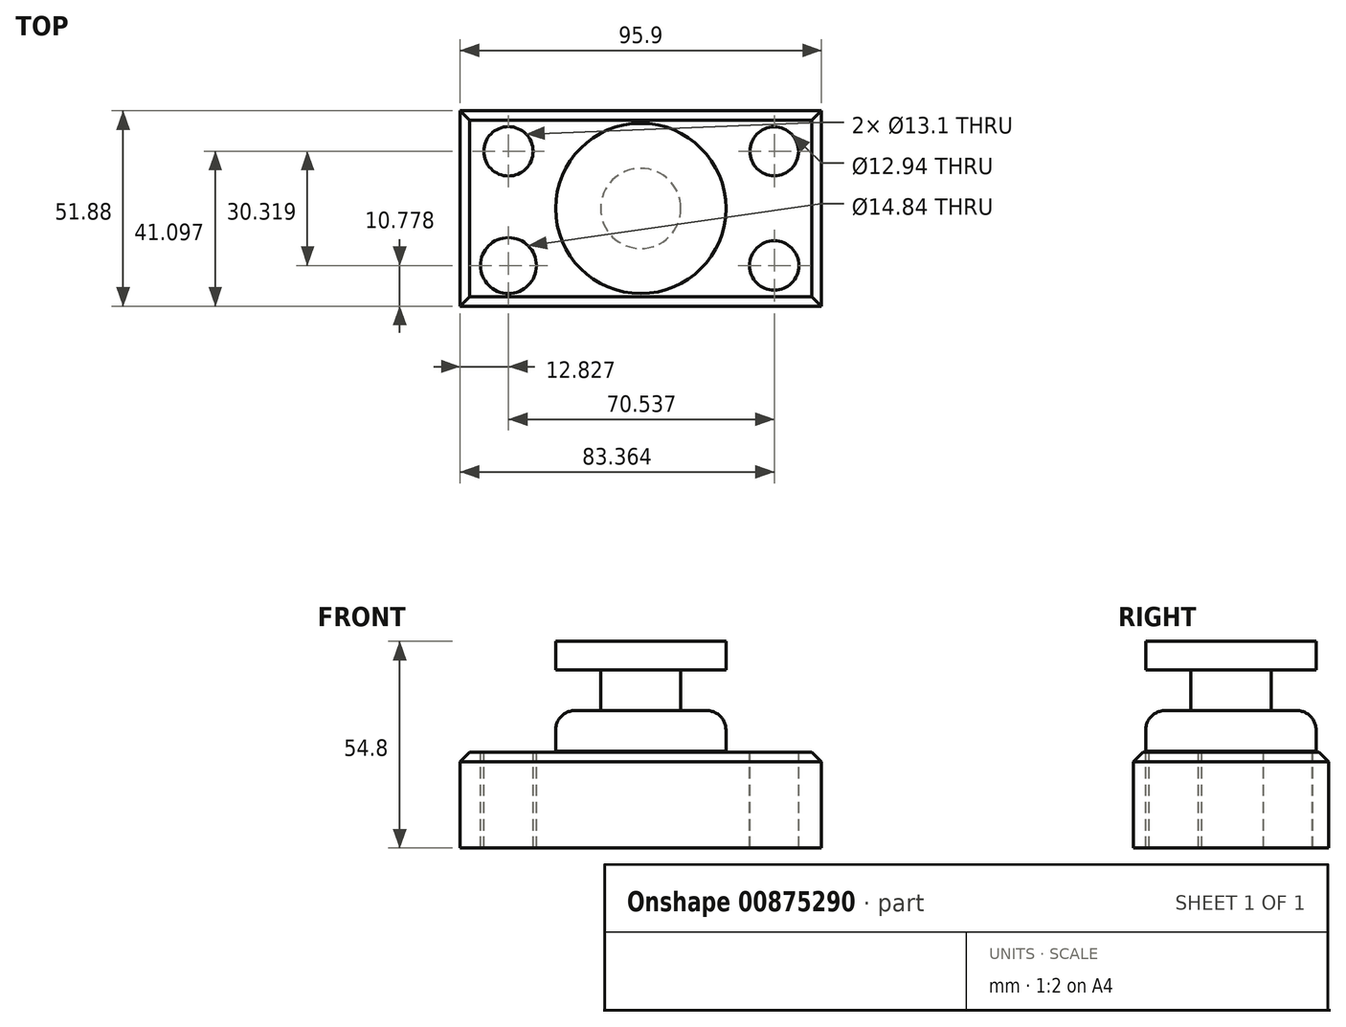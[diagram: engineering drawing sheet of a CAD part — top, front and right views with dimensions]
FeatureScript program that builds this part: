
annotation { "Feature Type Name" : "Feature", "Feature Type Description" : "" }
export const myFeature = defineFeature(function(context is Context, id is Id, definition is map)
    precondition{}
    {
        {
            var Q0;
            Q0=qCreatedBy(makeId("Top.planeOp"),FACE);
            var sketch = newSketch(context, id + "F0", { "sketchPlane" : qUnion([Q0])});
            skLineSegment(sketch, "E0.bottom", {"start": v(47.95, 25.94) * mm, "end": v(-47.95, 25.94) * mm});
            skLineSegment(sketch, "E0.top", {"start": v(47.95, -25.94) * mm, "end": v(-47.95, -25.94) * mm});
            skLineSegment(sketch, "E0.left", {"start": v(47.95, 25.94) * mm, "end": v(47.95, -25.94) * mm});
            skLineSegment(sketch, "E0.right", {"start": v(-47.95, 25.94) * mm, "end": v(-47.95, -25.94) * mm});
            skPoint(sketch, "E0.middle", {"position": v(0, 0) * mm});
            skSolve(sketch);
        }
        {
            var Q0;
            Q0=makeQuery(id+"F0.imprint","IMPRINT",FACE,{"disambiguationData":[TD([[makeQuery(id+"F0.imprint","IMPRINT",EDGE,{"derivedFrom":sQuery(id+"F0.wireOp",EDGE,"E0.bottom")}),1.0]])]});
            extrude(context, id + "F1", {"entities" : qUnion([Q0]), "depth" : 25.4 * mm, "offsetDistance" : 25.4 * mm});
        }
        {
            var Q0;
            Q0=makeQuery(id+"F1.opExtrude","CAP_FACE",FACE,{"disambiguationData":[OSD([sQuery(id+"F0.wireOp",EDGE,"E0.bottom"),sQuery(id+"F0.wireOp",EDGE,"E0.top"),sQuery(id+"F0.wireOp",EDGE,"E0.left"),sQuery(id+"F0.wireOp",EDGE,"E0.right")])],"isStart":false});
            var sketch = newSketch(context, id + "F2", { "sketchPlane" : qUnion([Q0])});
            skCircle(sketch, "E1", {"center": v(-35.12, 15.16) * mm, "radius": 6.55 * mm});
            skCircle(sketch, "E2", {"center": v(35.41, 15.16) * mm, "radius": 6.47 * mm});
            skCircle(sketch, "E3", {"center": v(-35.12, -15.16) * mm, "radius": 7.42 * mm});
            skCircle(sketch, "E4", {"center": v(35.41, -15.16) * mm, "radius": 6.55 * mm});
            skSolve(sketch);
        }
        {
            var Q0;
            Q0=makeQuery(id+"F2.imprint","IMPRINT",FACE,{"disambiguationData":[TD([[makeQuery(id+"F2.imprint","IMPRINT",EDGE,{"derivedFrom":sQuery(id+"F2.wireOp",EDGE,"E1")}),1.0]])]});
            var Q1;
            Q1=makeQuery(id+"F2.imprint","IMPRINT",FACE,{"disambiguationData":[TD([[makeQuery(id+"F2.imprint","IMPRINT",EDGE,{"derivedFrom":sQuery(id+"F2.wireOp",EDGE,"E2")}),1.0]])]});
            var Q2;
            Q2=makeQuery(id+"F2.imprint","IMPRINT",FACE,{"disambiguationData":[TD([[makeQuery(id+"F2.imprint","IMPRINT",EDGE,{"derivedFrom":sQuery(id+"F2.wireOp",EDGE,"E4")}),1.0]])]});
            var Q3;
            Q3=makeQuery(id+"F2.imprint","IMPRINT",FACE,{"disambiguationData":[TD([[makeQuery(id+"F2.imprint","IMPRINT",EDGE,{"derivedFrom":sQuery(id+"F2.wireOp",EDGE,"E3")}),1.0]])]});
            extrude(context, id + "F3", {"entities" : qUnion([Q0, Q1, Q2, Q3]), "operationType" : NewBodyOperationType.REMOVE, "oppositeDirection" : true, "depth" : 25.4 * mm, "offsetDistance" : 25.4 * mm});
        }
        {
            var Q0;
            Q0=qCreatedBy(makeId("Front.planeOp"),FACE);
            var sketch = newSketch(context, id + "F4", { "sketchPlane" : qUnion([Q0])});
            skLineSegment(sketch, "E5", {"start": v(0, 0) * mm, "end": v(0, 54.8) * mm});
            skLineSegment(sketch, "E6", {"start": v(0, 54.8) * mm, "end": v(22.59, 54.8) * mm});
            skLineSegment(sketch, "E7", {"start": v(22.59, 54.8) * mm, "end": v(22.59, 47.22) * mm});
            skLineSegment(sketch, "E8", {"start": v(22.59, 47.22) * mm, "end": v(10.64, 47.22) * mm});
            skLineSegment(sketch, "E9", {"start": v(10.64, 47.22) * mm, "end": v(10.64, 36.43) * mm});
            skLineSegment(sketch, "E10", {"start": v(10.64, 36.43) * mm, "end": v(22.59, 36.43) * mm});
            skLineSegment(sketch, "E11", {"start": v(22.59, 36.43) * mm, "end": v(22.59, 25.65) * mm});
            skLineSegment(sketch, "E12", {"start": v(22.59, 25.65) * mm, "end": v(0, 25.65) * mm});
            skSolve(sketch);
        }
        {
            var Q0;
            Q0=makeQuery(id+"F1.opExtrude","CAP_EDGE",EDGE,{"disambiguationData":[OSD([sQuery(id+"F0.wireOp",EDGE,"E0.top")])],"isStart":false});
            var Q1;
            Q1=makeQuery(id+"F1.opExtrude","CAP_EDGE",EDGE,{"disambiguationData":[OSD([sQuery(id+"F0.wireOp",EDGE,"E0.right")])],"isStart":false});
            var Q2;
            Q2=makeQuery(id+"F1.opExtrude","CAP_EDGE",EDGE,{"disambiguationData":[OSD([sQuery(id+"F0.wireOp",EDGE,"E0.left")])],"isStart":false});
            var Q3;
            Q3=makeQuery(id+"F1.opExtrude","CAP_EDGE",EDGE,{"disambiguationData":[OSD([sQuery(id+"F0.wireOp",EDGE,"E0.bottom")])],"isStart":false});
            chamfer(context, id + "F5", {"entities" : qUnion([Q0, Q1, Q2, Q3]), "width" : 2.54 * mm, "tangentPropagation" : true});
        }
        {
            var Q0;
            {var subQ0=sQuery(id+"F4.wireOp",EDGE,"E6");Q0=makeQuery(id+"F4.imprint","IMPRINT",FACE,{"disambiguationData":[TD([[makeQuery(id+"F4.imprint","IMPRINT",EDGE,{"derivedFrom":subQ0}),-1.0]])]});}
            var Q1;
            Q1=sQuery(id+"F4.wireOp",EDGE,"E5");
            revolve(context, id + "F6", {"surfaceOperationType" : NewSurfaceOperationType.NEW, "entities" : qUnion([Q0]), "axis" : qUnion([Q1]), "revolveType" : RevolveType.FULL});
        }
        {
            var Q0;
            Q0=makeQuery(id+"F6.opRevolve","SWEPT_EDGE",EDGE,{"disambiguationData":[OSD([sQuery(id+"F4.wireOp",EDGE,"E10"),sQuery(id+"F4.wireOp",EDGE,"E11")])]});
            fillet(context, id + "F7", {"entities" : qUnion([Q0]), "radius" : 5.08 * mm, "tangentPropagation" : true, "allowEdgeOverflow" : false});
        }
    });
